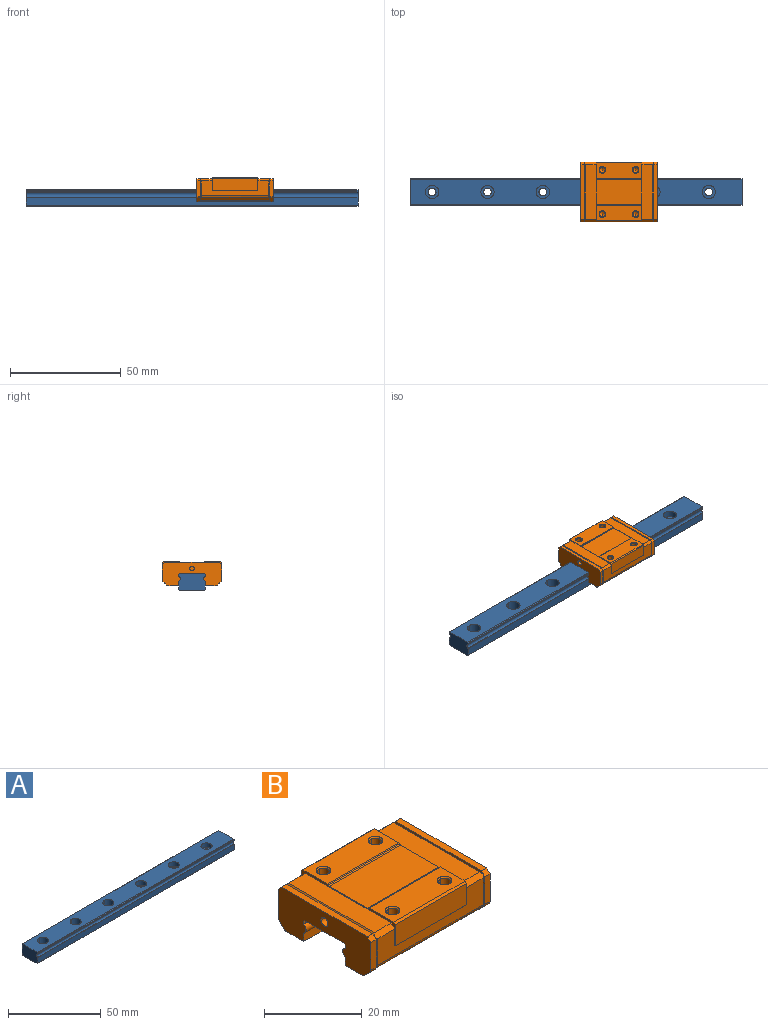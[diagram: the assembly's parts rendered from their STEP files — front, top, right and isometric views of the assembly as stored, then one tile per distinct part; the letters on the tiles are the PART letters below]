
ASSEMBLY  parts=2 mates=2
PART A: 42 faces, bbox 150x12x7.5 mm
  f0: cylinder r=1.75mm len=4.5mm, axis (0,0,1), area 49.5mm2, adj f12,f40
  f1: cylinder r=1.75mm len=4.5mm, axis (0,0,1), area 49.5mm2, adj f12,f38
  f2: cylinder r=1.75mm len=4.5mm, axis (0,0,1), area 49.5mm2, adj f12,f36
  f3: plane 150x0.3mm, normal (0,-0.71,0.71), area 63.6mm2, adj f4,f17,f19,f35
  f4: plane 150x11.4mm, normal (0,0,1), area 1540.4mm2, adj f3,f5,f17,f23,f24,f28,f29,f33
  f5: plane 150x0.3mm, normal (0,0.71,0.71), area 63.6mm2, adj f4,f6,f17,f35
  f6: plane 150x0.69mm, normal (0,1,0), area 103.1mm2, adj f5,f7,f17,f35
  f7: cylinder r=0.15mm len=150mm, axis (1,0,0), area 23.6mm2, adj f6,f8,f17,f35
  f8: cylinder r=1.25mm len=150mm, axis (1,0,0), area 392.7mm2, adj f7,f9,f17,f35
  f9: cylinder r=0.15mm len=150mm, axis (1,0,0), area 23.6mm2, adj f8,f10,f17,f35
  f10: plane 150x3.59mm, normal (0,1,0), area 538.1mm2, adj f9,f11,f17,f35
  f11: plane 150x0.5mm, normal (0,0.71,-0.71), area 106.1mm2, adj f10,f12,f17,f35
  f12: plane 150x11mm, normal (0,0,-1), area 1592.3mm2, adj f0,f1,f2,f11,f13,f17,f20,f21
  f13: plane 150x0.5mm, normal (0,-0.71,-0.71), area 106.1mm2, adj f12,f14,f17,f35
  f14: plane 150x3.59mm, normal (0,-1,0), area 538.1mm2, adj f13,f15,f17,f35
  f15: cylinder r=0.15mm len=150mm, axis (1,0,0), area 23.6mm2, adj f14,f16,f17,f35
  f16: cylinder r=1.25mm len=150mm, axis (1,0,0), area 392.7mm2, adj f15,f17,f18,f35
  f17: plane 12x7.5mm, normal (-1,0,0), area 87.4mm2, adj f3,f4,f5,f6,f7,f8,f9,f10
  f18: cylinder r=0.15mm len=150mm, axis (1,0,0), area 23.6mm2, adj f16,f17,f19,f35
  f19: plane 150x0.69mm, normal (0,-1,0), area 103.1mm2, adj f3,f17,f18,f35
  f20: cylinder r=1.75mm len=3.5mm, axis (0,0,1), area 16.5mm2, adj f12,f21,f22
  f21: cylinder r=1.75mm len=3.5mm, axis (0,0,1), area 16.5mm2, adj f12,f20,f22
  f22: plane 6x6mm, normal (0,0,1), area 18.7mm2, adj f20,f21,f23,f24
  f23: cylinder r=3mm len=6mm, axis (0,0,1), area 42.4mm2, adj f4,f22,f24
  f24: cylinder r=3mm len=6mm, axis (0,0,1), area 42.4mm2, adj f4,f22,f23
  f25: cylinder r=1.75mm len=3.5mm, axis (0,0,1), area 16.5mm2, adj f12,f26,f27
  f26: cylinder r=1.75mm len=3.5mm, axis (0,0,1), area 16.5mm2, adj f12,f25,f27
  f27: plane 6x6mm, normal (0,0,1), area 18.7mm2, adj f25,f26,f28,f29
  f28: cylinder r=3mm len=6mm, axis (0,0,1), area 42.4mm2, adj f4,f27,f29
  f29: cylinder r=3mm len=6mm, axis (0,0,1), area 42.4mm2, adj f4,f27,f28
  f30: cylinder r=1.75mm len=3.5mm, axis (0,0,1), area 16.5mm2, adj f12,f31,f32
  f31: cylinder r=1.75mm len=3.5mm, axis (0,0,1), area 16.5mm2, adj f12,f30,f32
  f32: plane 6x6mm, normal (0,0,1), area 18.7mm2, adj f30,f31,f33,f34
  f33: cylinder r=3mm len=6mm, axis (0,0,1), area 42.4mm2, adj f4,f32,f34
  f34: cylinder r=3mm len=6mm, axis (0,0,1), area 42.4mm2, adj f4,f32,f33
  f35: plane 12x7.5mm, normal (1,0,0), area 87.4mm2, adj f3,f4,f5,f6,f7,f8,f9,f10
  f36: plane 6x6mm, normal (0,0,1), area 18.7mm2, adj f2,f37
  f37: cylinder r=3mm len=6mm, axis (0,0,1), area 56.5mm2, adj f4,f36
  f38: plane 6x6mm, normal (0,0,1), area 18.7mm2, adj f1,f39
  f39: cylinder r=3mm len=6mm, axis (0,0,1), area 56.5mm2, adj f4,f38
  f40: plane 6x6mm, normal (0,0,1), area 18.7mm2, adj f0,f41
  f41: cylinder r=3mm len=6mm, axis (0,0,1), area 56.5mm2, adj f4,f40
PART B: 128 faces, bbox 34.4x27x11 mm
  f0: plane 0.44x0.05mm, normal (-1,0,0), area 0mm2, adj f1,f85
  f1: plane 30.4x6.69mm, normal (0,1,0), area 115.5mm2, adj f0,f2,f9,f10,f32,f34,f63,f86
  f2: plane 5.4x1mm, normal (0,0.71,0.71), area 7.3mm2, adj f1,f3,f4,f32,f90
  f3: plane 25.8x0.5mm, normal (0.71,0,0.71), area 17.9mm2, adj f2,f4,f5,f27
  f4: plane 24.8x4.9mm, normal (0,0,1), area 121.5mm2, adj f2,f3,f5,f90
  f5: plane 5.4x1mm, normal (0,-0.71,0.71), area 7.3mm2, adj f3,f4,f6,f24,f90
  f6: plane 30.4x6.69mm, normal (0,-1,0), area 115.5mm2, adj f5,f7,f9,f24,f68,f69,f90,f91
  f7: plane 5.4x1mm, normal (0,-0.71,0.71), area 7.3mm2, adj f6,f8,f9,f11,f69
  f8: plane 24.8x4.9mm, normal (0,0,1), area 121.5mm2, adj f7,f9,f10,f11
  f9: plane 27x5.76mm, normal (-1,0,0), area 11.6mm2, adj f1,f6,f7,f8,f10,f85,f91,f92
  f10: plane 5.4x1mm, normal (0,0.71,0.71), area 7.3mm2, adj f1,f8,f9,f11,f34
  f11: plane 25.8x0.5mm, normal (-0.71,0,0.71), area 17.9mm2, adj f7,f8,f10,f12
  f12: plane 25.8x0.5mm, normal (1,0,0), area 12.7mm2, adj f11,f13,f38,f39
  f13: plane 1.5x1mm, normal (0,-0.71,0.71), area 2.1mm2, adj f12,f14,f39,f70,f78
  f14: plane 26.8x10.4mm, normal (-1,0,0), area 207.6mm2, adj f13,f15,f36,f37,f38,f39,f40,f41
  f15: cylinder r=0.15mm len=34.4mm, axis (1,0,0), area 5.4mm2, adj f14,f16,f59,f77
  f16: plane 26.8x10.4mm, normal (1,0,0), area 207.6mm2, adj f15,f17,f18,f26,f28,f29,f30,f49
  f17: cylinder r=1mm len=1.5mm, axis (1,0,0), area 1.2mm2, adj f16,f18,f25,f67
  f18: plane 4.89x1.5mm, normal (0,0,-1), area 7.3mm2, adj f16,f17,f19,f25,f77
  f19: plane 0.19x0.1mm, normal (1,0,0), area 0mm2, adj f18,f20,f76,f77
  f20: plane 31.4x0.3mm, normal (0,-0.71,-0.71), area 13.3mm2, adj f19,f21,f25,f70,f75,f76
  f21: plane 31.4x4.5mm, normal (0,0,-1), area 141.2mm2, adj f20,f22,f25,f70
  f22: cylinder r=1mm len=31.4mm, axis (1,0,0), area 24.7mm2, adj f21,f23,f25,f70
  f23: plane 31.4x1.51mm, normal (0,-0.71,-0.71), area 67.2mm2, adj f22,f24,f25,f68,f69,f70
  f24: plane 8.1x0.5mm, normal (0.71,-0.71,0), area 5.3mm2, adj f5,f6,f23,f25,f68
  f25: plane 9.9x7.21mm, normal (-1,0,0), area 5.2mm2, adj f17,f18,f20,f21,f22,f23,f24,f26
  f26: plane 1.5x1mm, normal (0,-0.71,0.71), area 2.1mm2, adj f16,f25,f27,f64,f65
  f27: plane 25.8x0.5mm, normal (-1,0,0), area 12.7mm2, adj f3,f26,f28,f64
  f28: plane 1.5x1mm, normal (0,0.71,0.71), area 2.1mm2, adj f16,f27,f29,f31,f64
  f29: plane 6.89x1.5mm, normal (0,1,0), area 10.3mm2, adj f16,f28,f30,f31
  f30: cylinder r=1mm len=1.5mm, axis (1,0,0), area 1.2mm2, adj f16,f29,f31,f62
  f31: plane 9.9x7.21mm, normal (-1,0,0), area 5.2mm2, adj f28,f29,f30,f32,f33,f46,f47,f48
  f32: plane 8.1x0.5mm, normal (0.71,0.71,0), area 5.3mm2, adj f1,f2,f31,f33,f63
  f33: plane 31.4x1.51mm, normal (0,0.71,-0.71), area 67.2mm2, adj f31,f32,f34,f35,f48,f63
  f34: plane 8.1x0.5mm, normal (-0.71,0.71,0), area 5.3mm2, adj f1,f10,f33,f35,f63
  f35: plane 9.9x7.21mm, normal (1,0,0), area 5.2mm2, adj f33,f34,f36,f37,f38,f40,f41,f42
  f36: cylinder r=1mm len=1.5mm, axis (1,0,0), area 1.2mm2, adj f14,f35,f37,f40
  f37: plane 6.89x1.5mm, normal (0,1,0), area 10.3mm2, adj f14,f35,f36,f38
  f38: plane 1.5x1mm, normal (0,0.71,0.71), area 2.1mm2, adj f12,f14,f35,f37,f39
  f39: plane 24.8x1.5mm, normal (0,0,1), area 37.2mm2, adj f12,f13,f14,f38
  f40: plane 1.51x1.51mm, normal (0,0.71,-0.71), area 3.2mm2, adj f14,f35,f36,f41
  f41: cylinder r=1mm len=1.5mm, axis (1,0,0), area 1.2mm2, adj f14,f35,f40,f42
  f42: plane 4.89x1.5mm, normal (0,0,-1), area 7.3mm2, adj f14,f35,f41,f43,f49
  f43: plane 0.19x0.1mm, normal (-1,0,0), area 0mm2, adj f42,f44,f46,f49
  f44: plane 31.4x0.09mm, normal (0,0,-1), area 2.8mm2, adj f43,f45,f46,f49
  f45: plane 0.19x0.1mm, normal (1,0,0), area 0mm2, adj f44,f46,f49,f60
  f46: plane 31.4x0.3mm, normal (0,0.71,-0.71), area 13.3mm2, adj f31,f35,f43,f44,f45,f47
  f47: plane 31.4x4.5mm, normal (0,0,-1), area 141.2mm2, adj f31,f35,f46,f48
  f48: cylinder r=1mm len=31.4mm, axis (1,0,0), area 24.7mm2, adj f31,f33,f35,f47
  f49: plane 34.4x2.09mm, normal (0,-1,0), area 71.5mm2, adj f14,f16,f42,f43,f44,f45,f50,f60
  f50: cylinder r=0.15mm len=34.4mm, axis (1,0,0), area 5.4mm2, adj f14,f16,f49,f51
  f51: cylinder r=1.25mm len=34.4mm, axis (1,0,0), area 90.1mm2, adj f14,f16,f50,f52
  f52: cylinder r=0.15mm len=34.4mm, axis (1,0,0), area 5.4mm2, adj f14,f16,f51,f53
  f53: plane 34.4x0.69mm, normal (0,-1,0), area 23.7mm2, adj f14,f16,f52,f54
  f54: plane 34.4x0.3mm, normal (0,-0.71,-0.71), area 14.6mm2, adj f14,f16,f53,f55
  f55: plane 34.4x11.4mm, normal (0,0,-1), area 392.2mm2, adj f14,f16,f54,f56
  f56: plane 34.4x0.3mm, normal (0,0.71,-0.71), area 14.6mm2, adj f14,f16,f55,f57
  f57: plane 34.4x0.69mm, normal (0,1,0), area 23.7mm2, adj f14,f16,f56,f58
  f58: cylinder r=0.15mm len=34.4mm, axis (1,0,0), area 5.4mm2, adj f14,f16,f57,f59
  f59: cylinder r=1.25mm len=34.4mm, axis (1,0,0), area 90.1mm2, adj f14,f15,f16,f58
  f60: plane 4.89x1.5mm, normal (0,0,-1), area 7.3mm2, adj f16,f31,f45,f49,f61
  f61: cylinder r=1mm len=1.5mm, axis (1,0,0), area 1.2mm2, adj f16,f31,f60,f62
  f62: plane 1.51x1.51mm, normal (0,0.71,-0.71), area 3.2mm2, adj f16,f30,f31,f61
  f63: cylinder r=1mm len=30.99mm, axis (1,0,0), area 24mm2, adj f1,f32,f33,f34
  f64: plane 24.8x1.5mm, normal (0,0,1), area 37.2mm2, adj f16,f26,f27,f28
  f65: plane 6.89x1.5mm, normal (0,-1,0), area 10.3mm2, adj f16,f25,f26,f66
  f66: cylinder r=1mm len=1.5mm, axis (1,0,0), area 1.2mm2, adj f16,f25,f65,f67
  f67: plane 1.51x1.51mm, normal (0,-0.71,-0.71), area 3.2mm2, adj f16,f17,f25,f66
  f68: cylinder r=1mm len=30.99mm, axis (1,0,0), area 24mm2, adj f6,f23,f24,f69
  f69: plane 8.1x0.5mm, normal (-0.71,-0.71,0), area 5.3mm2, adj f6,f7,f23,f68,f70
  f70: plane 9.9x7.21mm, normal (1,0,0), area 5.2mm2, adj f13,f20,f21,f22,f23,f69,f71,f72
  f71: cylinder r=1mm len=1.5mm, axis (1,0,0), area 1.2mm2, adj f14,f70,f72,f78
  f72: plane 1.51x1.51mm, normal (0,-0.71,-0.71), area 3.2mm2, adj f14,f70,f71,f73
  f73: cylinder r=1mm len=1.5mm, axis (1,0,0), area 1.2mm2, adj f14,f70,f72,f74
  f74: plane 4.89x1.5mm, normal (0,0,-1), area 7.3mm2, adj f14,f70,f73,f75,f77
  f75: plane 0.19x0.1mm, normal (-1,0,0), area 0mm2, adj f20,f74,f76,f77
  f76: plane 31.4x0.09mm, normal (0,0,-1), area 2.8mm2, adj f19,f20,f75,f77
  f77: plane 34.4x2.09mm, normal (0,1,0), area 71.5mm2, adj f14,f15,f16,f18,f19,f74,f75,f76
  f78: plane 6.89x1.5mm, normal (0,-1,0), area 10.3mm2, adj f13,f14,f70,f71
  f79: cylinder r=1mm len=4mm, axis (-1,0,0), area 12.6mm2, adj f16,f80,f81
  f80: cylinder r=1mm len=4mm, axis (-1,0,0), area 12.6mm2, adj f16,f79,f81
  f81: plane 2x2mm, normal (1,0,0), area 3.1mm2, adj f79,f80
  f82: cylinder r=1mm len=4mm, axis (-1,0,0), area 12.6mm2, adj f14,f83,f84
  f83: cylinder r=1mm len=4mm, axis (-1,0,0), area 12.6mm2, adj f14,f82,f84
  f84: plane 2x2mm, normal (-1,0,0), area 3.1mm2, adj f82,f83
  f85: cylinder r=0.5mm len=20.6mm, axis (1,0,0), area 16.4mm2, adj f0,f9,f86,f87,f89,f90,f102,f127
  f86: plane 1.94x0.1mm, normal (-1,0,0), area 0.2mm2, adj f1,f85,f87,f88
  f87: plane 20.6x1.74mm, normal (0,1,0), area 35.9mm2, adj f85,f86,f88,f89
  f88: plane 20.6x0.1mm, normal (0,0.51,-0.86), area 2.4mm2, adj f1,f86,f87,f89
  f89: plane 1.94x0.1mm, normal (1,0,0), area 0.2mm2, adj f1,f85,f87,f88
  f90: plane 27x5.76mm, normal (1,0,0), area 11.6mm2, adj f1,f2,f4,f5,f6,f85,f91,f92
  f91: plane 20.6x0.1mm, normal (0,-0.51,-0.86), area 2.4mm2, adj f6,f9,f90,f92
  f92: plane 20.6x5.3mm, normal (0,-1,0), area 109.2mm2, adj f9,f90,f91,f93
  f93: plane 20.6x0.4mm, normal (0,-0.71,0.71), area 11.7mm2, adj f9,f90,f92,f94
  f94: plane 20.6x7.1mm, normal (0,0,1), area 132.1mm2, adj f9,f90,f93,f95,f115,f116,f121,f122
  f95: plane 20.6x0.15mm, normal (0,0.71,0.71), area 4.5mm2, adj f9,f90,f94,f96
  f96: cylinder r=0.5mm len=20.6mm, axis (1,0,0), area 8.1mm2, adj f9,f90,f95,f97
  f97: plane 20.6x10.99mm, normal (0,0,1), area 226.3mm2, adj f9,f90,f96,f98
  f98: cylinder r=0.5mm len=20.6mm, axis (1,0,0), area 8.1mm2, adj f9,f90,f97,f99
  f99: plane 20.6x0.15mm, normal (0,-0.71,0.71), area 4.5mm2, adj f9,f90,f98,f100
  f100: plane 20.6x7.1mm, normal (0,0,1), area 132.1mm2, adj f9,f90,f99,f101,f103,f104,f109,f110
  f101: plane 20.6x0.4mm, normal (0,0.71,0.71), area 11.7mm2, adj f9,f90,f100,f102
  f102: plane 20.6x2.84mm, normal (0,1,0), area 58.6mm2, adj f9,f85,f90,f101
  f103: cone r=1.5mm half-angle=45deg, axis (0,0,1), area 1.6mm2, adj f100,f104,f106
  f104: cone r=1.5mm half-angle=45deg, axis (0,0,1), area 1.6mm2, adj f100,f103,f105
  f105: cylinder r=1.23mm len=3.57mm, axis (0,0,1), area 13.8mm2, adj f104,f106,f108
  f106: cylinder r=1.23mm len=3.57mm, axis (0,0,1), area 13.8mm2, adj f103,f105,f107
  f107: cone r=1.23mm half-angle=60deg, axis (0,0,1), area 2.7mm2, adj f106,f108
  f108: cone r=1.23mm half-angle=60deg, axis (0,0,1), area 2.7mm2, adj f105,f107
  f109: cone r=1.5mm half-angle=45deg, axis (0,0,1), area 1.6mm2, adj f100,f110,f112
  f110: cone r=1.5mm half-angle=45deg, axis (0,0,1), area 1.6mm2, adj f100,f109,f111
  f111: cylinder r=1.23mm len=3.57mm, axis (0,0,1), area 13.8mm2, adj f110,f112,f114
  f112: cylinder r=1.23mm len=3.57mm, axis (0,0,1), area 13.8mm2, adj f109,f111,f113
  f113: cone r=1.23mm half-angle=60deg, axis (0,0,1), area 2.7mm2, adj f112,f114
  f114: cone r=1.23mm half-angle=60deg, axis (0,0,1), area 2.7mm2, adj f111,f113
  f115: cone r=1.5mm half-angle=45deg, axis (0,0,1), area 1.6mm2, adj f94,f116,f118
  f116: cone r=1.5mm half-angle=45deg, axis (0,0,1), area 1.6mm2, adj f94,f115,f117
  f117: cylinder r=1.23mm len=3.57mm, axis (0,0,1), area 13.8mm2, adj f116,f118,f120
  f118: cylinder r=1.23mm len=3.57mm, axis (0,0,1), area 13.8mm2, adj f115,f117,f119
  f119: cone r=1.23mm half-angle=60deg, axis (0,0,1), area 2.7mm2, adj f118,f120
  f120: cone r=1.23mm half-angle=60deg, axis (0,0,1), area 2.7mm2, adj f117,f119
  f121: cone r=1.5mm half-angle=45deg, axis (0,0,1), area 1.6mm2, adj f94,f122,f124
  f122: cone r=1.5mm half-angle=45deg, axis (0,0,1), area 1.6mm2, adj f94,f121,f123
  f123: cylinder r=1.23mm len=3.57mm, axis (0,0,1), area 13.8mm2, adj f122,f124,f126
  f124: cylinder r=1.23mm len=3.57mm, axis (0,0,1), area 13.8mm2, adj f121,f123,f125
  f125: cone r=1.23mm half-angle=60deg, axis (0,0,1), area 2.7mm2, adj f124,f126
  f126: cone r=1.23mm half-angle=60deg, axis (0,0,1), area 2.7mm2, adj f123,f125
  f127: plane 0.44x0.05mm, normal (1,0,0), area 0mm2, adj f1,f85
PLACE A t=(-32.15,40.94,63.85)mm fixed
PLACE B t=(52.3,40.94,65.85)mm
MATE parallel B.f55 <-> A.f4  axis (0,0,-1) through (52.3,40.94,71.35)mm
MATE parallel B.f49 <-> A.f10  axis (0,-1,0) through (52.3,46.94,65.85)mm
